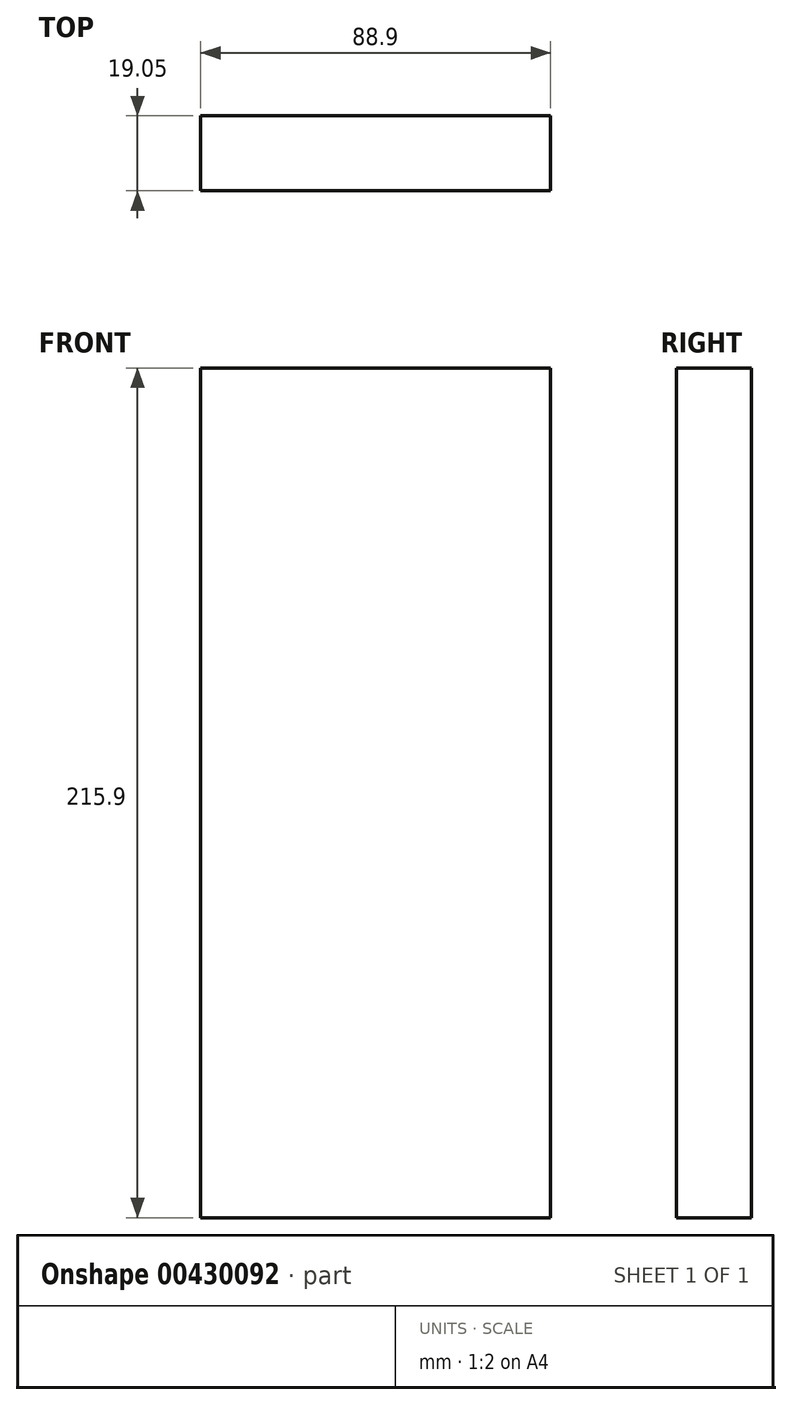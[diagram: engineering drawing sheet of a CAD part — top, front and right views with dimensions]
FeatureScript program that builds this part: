
annotation { "Feature Type Name" : "Feature", "Feature Type Description" : "" }
export const myFeature = defineFeature(function(context is Context, id is Id, definition is map)
    precondition{}
    {
        {
            var Q0;
            Q0=qCreatedBy(makeId("Top.planeOp"),FACE);
            var sketch = newSketch(context, id + "F0", { "sketchPlane" : qUnion([Q0])});
            skLineSegment(sketch, "E0.bottom", {"start": v(0, 0) * mm, "end": v(88.9, 0) * mm});
            skLineSegment(sketch, "E0.top", {"start": v(0, -19.05) * mm, "end": v(88.9, -19.05) * mm});
            skLineSegment(sketch, "E0.left", {"start": v(0, 0) * mm, "end": v(0, -19.05) * mm});
            skLineSegment(sketch, "E0.right", {"start": v(88.9, 0) * mm, "end": v(88.9, -19.05) * mm});
            skSolve(sketch);
        }
        {
            var Q0;
            Q0=makeQuery(id+"F0.imprint","IMPRINT",FACE,{"disambiguationData":[TD([[makeQuery(id+"F0.imprint","IMPRINT",EDGE,{"derivedFrom":sQuery(id+"F0.wireOp",EDGE,"E0.bottom")}),-1.0]])]});
            extrude(context, id + "F1", {"entities" : qUnion([Q0]), "depth" : 215.9 * mm});
        }
    });
